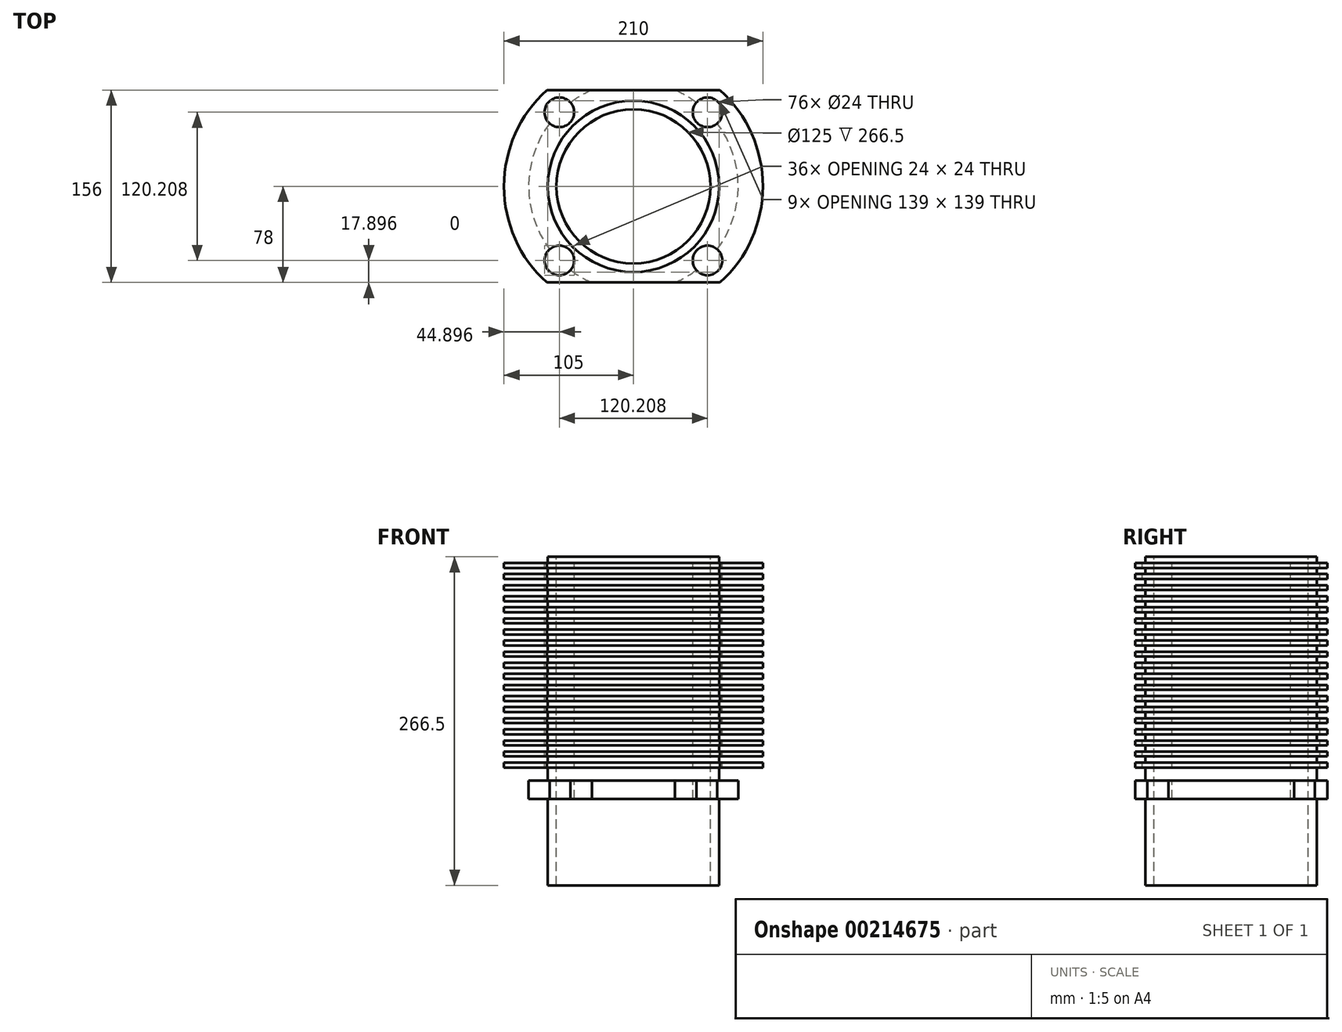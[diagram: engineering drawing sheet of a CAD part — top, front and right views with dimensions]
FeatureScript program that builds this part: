
annotation { "Feature Type Name" : "Feature", "Feature Type Description" : "" }
export const myFeature = defineFeature(function(context is Context, id is Id, definition is map)
    precondition{}
    {
        {
            var Q0;
            Q0=qCreatedBy(makeId("Top.planeOp"),FACE);
            var sketch = newSketch(context, id + "F0", { "sketchPlane" : qUnion([Q0])});
            skCircle(sketch, "E0", {"center": v(0, 0) * mm, "radius": 69.5 * mm});
            skCircle(sketch, "E1", {"center": v(0, 0) * mm, "radius": 62.5 * mm});
            skSolve(sketch);
        }
        {
            var Q0;
            Q0=makeQuery(id+"F0.imprint","IMPRINT",FACE,{"disambiguationData":[TD([[makeQuery(id+"F0.imprint","IMPRINT",EDGE,{"derivedFrom":sQuery(id+"F0.wireOp",EDGE,"E0")}),1.0]])]});
            extrude(context, id + "F1", {"entities" : qUnion([Q0]), "oppositeDirection" : true, "depth" : 266.5 * mm});
        }
        {
            var Q0;
            Q0=qCreatedBy(makeId("Front.planeOp"),FACE);
            var sketch = newSketch(context, id + "F2", { "sketchPlane" : qUnion([Q0])});
            skLineSegment(sketch, "E2", {"start": v(0, 0) * mm, "end": v(0, -266.5) * mm});
            skLineSegment(sketch, "E3", {"start": v(0, -196.5) * mm, "end": v(85, -196.5) * mm});
            skLineSegment(sketch, "E4", {"start": v(85, -196.5) * mm, "end": v(85, -181.5) * mm});
            skLineSegment(sketch, "E5", {"start": v(85, -181.5) * mm, "end": v(0, -181.5) * mm});
            skLineSegment(sketch, "E6", {"start": v(0, -5) * mm, "end": v(105, -5) * mm});
            skLineSegment(sketch, "E7", {"start": v(105, -5) * mm, "end": v(105, -9) * mm});
            skLineSegment(sketch, "E8", {"start": v(105, -9) * mm, "end": v(0, -9) * mm});
            skLineSegment(sketch, "E9.0.1.0", {"start": v(0, -14) * mm, "end": v(105, -14) * mm});
            skLineSegment(sketch, "E9.0.1.1", {"start": v(105, -18) * mm, "end": v(0, -18) * mm});
            skLineSegment(sketch, "E9.0.1.2", {"start": v(105, -14) * mm, "end": v(105, -18) * mm});
            skLineSegment(sketch, "E9.0.2.0", {"start": v(0, -23) * mm, "end": v(105, -23) * mm});
            skLineSegment(sketch, "E9.0.2.1", {"start": v(105, -27) * mm, "end": v(0, -27) * mm});
            skLineSegment(sketch, "E9.0.2.2", {"start": v(105, -23) * mm, "end": v(105, -27) * mm});
            skLineSegment(sketch, "E9.0.3.0", {"start": v(0, -32) * mm, "end": v(105, -32) * mm});
            skLineSegment(sketch, "E9.0.3.1", {"start": v(105, -36) * mm, "end": v(0, -36) * mm});
            skLineSegment(sketch, "E9.0.3.2", {"start": v(105, -32) * mm, "end": v(105, -36) * mm});
            skLineSegment(sketch, "E9.0.4.0", {"start": v(0, -41) * mm, "end": v(105, -41) * mm});
            skLineSegment(sketch, "E9.0.4.1", {"start": v(105, -45) * mm, "end": v(0, -45) * mm});
            skLineSegment(sketch, "E9.0.4.2", {"start": v(105, -41) * mm, "end": v(105, -45) * mm});
            skLineSegment(sketch, "E9.0.5.0", {"start": v(0, -50) * mm, "end": v(105, -50) * mm});
            skLineSegment(sketch, "E9.0.5.1", {"start": v(105, -54) * mm, "end": v(0, -54) * mm});
            skLineSegment(sketch, "E9.0.5.2", {"start": v(105, -50) * mm, "end": v(105, -54) * mm});
            skLineSegment(sketch, "E9.0.6.0", {"start": v(0, -59) * mm, "end": v(105, -59) * mm});
            skLineSegment(sketch, "E9.0.6.1", {"start": v(105, -63) * mm, "end": v(0, -63) * mm});
            skLineSegment(sketch, "E9.0.6.2", {"start": v(105, -59) * mm, "end": v(105, -63) * mm});
            skLineSegment(sketch, "E9.0.7.0", {"start": v(0, -68) * mm, "end": v(105, -68) * mm});
            skLineSegment(sketch, "E9.0.7.1", {"start": v(105, -72) * mm, "end": v(0, -72) * mm});
            skLineSegment(sketch, "E9.0.7.2", {"start": v(105, -68) * mm, "end": v(105, -72) * mm});
            skLineSegment(sketch, "E9.0.8.0", {"start": v(0, -77) * mm, "end": v(105, -77) * mm});
            skLineSegment(sketch, "E9.0.8.1", {"start": v(105, -81) * mm, "end": v(0, -81) * mm});
            skLineSegment(sketch, "E9.0.8.2", {"start": v(105, -77) * mm, "end": v(105, -81) * mm});
            skLineSegment(sketch, "E9.0.9.0", {"start": v(0, -86) * mm, "end": v(105, -86) * mm});
            skLineSegment(sketch, "E9.0.9.1", {"start": v(105, -90) * mm, "end": v(0, -90) * mm});
            skLineSegment(sketch, "E9.0.9.2", {"start": v(105, -86) * mm, "end": v(105, -90) * mm});
            skLineSegment(sketch, "E9.0.10.0", {"start": v(0, -95) * mm, "end": v(105, -95) * mm});
            skLineSegment(sketch, "E9.0.10.1", {"start": v(105, -99) * mm, "end": v(0, -99) * mm});
            skLineSegment(sketch, "E9.0.10.2", {"start": v(105, -95) * mm, "end": v(105, -99) * mm});
            skLineSegment(sketch, "E9.0.11.0", {"start": v(0, -104) * mm, "end": v(105, -104) * mm});
            skLineSegment(sketch, "E9.0.11.1", {"start": v(105, -108) * mm, "end": v(0, -108) * mm});
            skLineSegment(sketch, "E9.0.11.2", {"start": v(105, -104) * mm, "end": v(105, -108) * mm});
            skLineSegment(sketch, "E9.0.12.0", {"start": v(0, -113) * mm, "end": v(105, -113) * mm});
            skLineSegment(sketch, "E9.0.12.1", {"start": v(105, -117) * mm, "end": v(0, -117) * mm});
            skLineSegment(sketch, "E9.0.12.2", {"start": v(105, -113) * mm, "end": v(105, -117) * mm});
            skLineSegment(sketch, "E9.0.13.0", {"start": v(0, -122) * mm, "end": v(105, -122) * mm});
            skLineSegment(sketch, "E9.0.13.1", {"start": v(105, -126) * mm, "end": v(0, -126) * mm});
            skLineSegment(sketch, "E9.0.13.2", {"start": v(105, -122) * mm, "end": v(105, -126) * mm});
            skLineSegment(sketch, "E9.0.14.0", {"start": v(0, -131) * mm, "end": v(105, -131) * mm});
            skLineSegment(sketch, "E9.0.14.1", {"start": v(105, -135) * mm, "end": v(0, -135) * mm});
            skLineSegment(sketch, "E9.0.14.2", {"start": v(105, -131) * mm, "end": v(105, -135) * mm});
            skLineSegment(sketch, "E9.direction1", {"start": v(0, -5) * mm, "end": v(31, -5) * mm, "construction": true});
            skLineSegment(sketch, "E9.direction2", {"start": v(0, -5) * mm, "end": v(0, -14) * mm, "construction": true});
            skLineSegment(sketch, "E10.0.0.15", {"start": v(0, -140) * mm, "end": v(105, -140) * mm});
            skLineSegment(sketch, "E10.3.0.15", {"start": v(105, -144) * mm, "end": v(0, -144) * mm});
            skLineSegment(sketch, "E10.6.0.15", {"start": v(105, -140) * mm, "end": v(105, -144) * mm});
            skLineSegment(sketch, "E10.0.0.16", {"start": v(0, -149) * mm, "end": v(105, -149) * mm});
            skLineSegment(sketch, "E10.3.0.16", {"start": v(105, -153) * mm, "end": v(0, -153) * mm});
            skLineSegment(sketch, "E10.6.0.16", {"start": v(105, -149) * mm, "end": v(105, -153) * mm});
            skLineSegment(sketch, "E10.0.0.17", {"start": v(0, -158) * mm, "end": v(105, -158) * mm});
            skLineSegment(sketch, "E10.3.0.17", {"start": v(105, -162) * mm, "end": v(0, -162) * mm});
            skLineSegment(sketch, "E10.6.0.17", {"start": v(105, -158) * mm, "end": v(105, -162) * mm});
            skLineSegment(sketch, "E10.0.0.18", {"start": v(0, -167) * mm, "end": v(105, -167) * mm});
            skLineSegment(sketch, "E10.3.0.18", {"start": v(105, -171) * mm, "end": v(0, -171) * mm});
            skLineSegment(sketch, "E10.6.0.18", {"start": v(105, -167) * mm, "end": v(105, -171) * mm});
            skSolve(sketch);
        }
        {
            var Q0;
            {var subQ0=sQuery(id+"F2.wireOp",EDGE,"E3");Q0=makeQuery(id+"F2.imprint","IMPRINT",FACE,{"disambiguationData":[TD([[makeQuery(id+"F2.imprint","IMPRINT",EDGE,{"derivedFrom":subQ0}),1.0]])]});}
            var Q1;
            {var subQ0=sQuery(id+"F2.wireOp",EDGE,"E10.0.0.18");Q1=makeQuery(id+"F2.imprint","IMPRINT",FACE,{"disambiguationData":[TD([[makeQuery(id+"F2.imprint","IMPRINT",EDGE,{"derivedFrom":subQ0}),-1.0]])]});}
            var Q2;
            {var subQ0=sQuery(id+"F2.wireOp",EDGE,"E10.0.0.17");Q2=makeQuery(id+"F2.imprint","IMPRINT",FACE,{"disambiguationData":[TD([[makeQuery(id+"F2.imprint","IMPRINT",EDGE,{"derivedFrom":subQ0}),-1.0]])]});}
            var Q3;
            {var subQ0=sQuery(id+"F2.wireOp",EDGE,"E10.0.0.16");Q3=makeQuery(id+"F2.imprint","IMPRINT",FACE,{"disambiguationData":[TD([[makeQuery(id+"F2.imprint","IMPRINT",EDGE,{"derivedFrom":subQ0}),-1.0]])]});}
            var Q4;
            {var subQ0=sQuery(id+"F2.wireOp",EDGE,"E10.0.0.15");Q4=makeQuery(id+"F2.imprint","IMPRINT",FACE,{"disambiguationData":[TD([[makeQuery(id+"F2.imprint","IMPRINT",EDGE,{"derivedFrom":subQ0}),-1.0]])]});}
            var Q5;
            {var subQ0=sQuery(id+"F2.wireOp",EDGE,"E9.0.14.0");Q5=makeQuery(id+"F2.imprint","IMPRINT",FACE,{"disambiguationData":[TD([[makeQuery(id+"F2.imprint","IMPRINT",EDGE,{"derivedFrom":subQ0}),-1.0]])]});}
            var Q6;
            {var subQ0=sQuery(id+"F2.wireOp",EDGE,"E9.0.13.0");Q6=makeQuery(id+"F2.imprint","IMPRINT",FACE,{"disambiguationData":[TD([[makeQuery(id+"F2.imprint","IMPRINT",EDGE,{"derivedFrom":subQ0}),-1.0]])]});}
            var Q7;
            {var subQ0=sQuery(id+"F2.wireOp",EDGE,"E9.0.12.0");Q7=makeQuery(id+"F2.imprint","IMPRINT",FACE,{"disambiguationData":[TD([[makeQuery(id+"F2.imprint","IMPRINT",EDGE,{"derivedFrom":subQ0}),-1.0]])]});}
            var Q8;
            {var subQ0=sQuery(id+"F2.wireOp",EDGE,"E9.0.11.0");Q8=makeQuery(id+"F2.imprint","IMPRINT",FACE,{"disambiguationData":[TD([[makeQuery(id+"F2.imprint","IMPRINT",EDGE,{"derivedFrom":subQ0}),-1.0]])]});}
            var Q9;
            {var subQ0=sQuery(id+"F2.wireOp",EDGE,"E9.0.10.0");Q9=makeQuery(id+"F2.imprint","IMPRINT",FACE,{"disambiguationData":[TD([[makeQuery(id+"F2.imprint","IMPRINT",EDGE,{"derivedFrom":subQ0}),-1.0]])]});}
            var Q10;
            {var subQ0=sQuery(id+"F2.wireOp",EDGE,"E9.0.9.0");Q10=makeQuery(id+"F2.imprint","IMPRINT",FACE,{"disambiguationData":[TD([[makeQuery(id+"F2.imprint","IMPRINT",EDGE,{"derivedFrom":subQ0}),-1.0]])]});}
            var Q11;
            {var subQ0=sQuery(id+"F2.wireOp",EDGE,"E9.0.8.0");Q11=makeQuery(id+"F2.imprint","IMPRINT",FACE,{"disambiguationData":[TD([[makeQuery(id+"F2.imprint","IMPRINT",EDGE,{"derivedFrom":subQ0}),-1.0]])]});}
            var Q12;
            {var subQ0=sQuery(id+"F2.wireOp",EDGE,"E9.0.7.0");Q12=makeQuery(id+"F2.imprint","IMPRINT",FACE,{"disambiguationData":[TD([[makeQuery(id+"F2.imprint","IMPRINT",EDGE,{"derivedFrom":subQ0}),-1.0]])]});}
            var Q13;
            {var subQ0=sQuery(id+"F2.wireOp",EDGE,"E9.0.6.0");Q13=makeQuery(id+"F2.imprint","IMPRINT",FACE,{"disambiguationData":[TD([[makeQuery(id+"F2.imprint","IMPRINT",EDGE,{"derivedFrom":subQ0}),-1.0]])]});}
            var Q14;
            {var subQ0=sQuery(id+"F2.wireOp",EDGE,"E9.0.5.0");Q14=makeQuery(id+"F2.imprint","IMPRINT",FACE,{"disambiguationData":[TD([[makeQuery(id+"F2.imprint","IMPRINT",EDGE,{"derivedFrom":subQ0}),-1.0]])]});}
            var Q15;
            {var subQ0=sQuery(id+"F2.wireOp",EDGE,"E9.0.4.0");Q15=makeQuery(id+"F2.imprint","IMPRINT",FACE,{"disambiguationData":[TD([[makeQuery(id+"F2.imprint","IMPRINT",EDGE,{"derivedFrom":subQ0}),-1.0]])]});}
            var Q16;
            {var subQ0=sQuery(id+"F2.wireOp",EDGE,"E9.0.3.0");Q16=makeQuery(id+"F2.imprint","IMPRINT",FACE,{"disambiguationData":[TD([[makeQuery(id+"F2.imprint","IMPRINT",EDGE,{"derivedFrom":subQ0}),-1.0]])]});}
            var Q17;
            {var subQ0=sQuery(id+"F2.wireOp",EDGE,"E9.0.2.0");Q17=makeQuery(id+"F2.imprint","IMPRINT",FACE,{"disambiguationData":[TD([[makeQuery(id+"F2.imprint","IMPRINT",EDGE,{"derivedFrom":subQ0}),-1.0]])]});}
            var Q18;
            {var subQ0=sQuery(id+"F2.wireOp",EDGE,"E9.0.1.0");Q18=makeQuery(id+"F2.imprint","IMPRINT",FACE,{"disambiguationData":[TD([[makeQuery(id+"F2.imprint","IMPRINT",EDGE,{"derivedFrom":subQ0}),-1.0]])]});}
            var Q19;
            {var subQ0=sQuery(id+"F2.wireOp",EDGE,"E6");Q19=makeQuery(id+"F2.imprint","IMPRINT",FACE,{"disambiguationData":[TD([[makeQuery(id+"F2.imprint","IMPRINT",EDGE,{"derivedFrom":subQ0}),-1.0]])]});}
            var Q20;
            Q20=sQuery(id+"F2.wireOp",EDGE,"E2");
            revolve(context, id + "F3", {"operationType" : NewBodyOperationType.ADD, "entities" : qUnion([Q0, Q1, Q2, Q3, Q4, Q5, Q6, Q7, Q8, Q9, Q10, Q11, Q12, Q13, Q14, Q15, Q16, Q17, Q18, Q19]), "axis" : qUnion([Q20]), "revolveType" : RevolveType.FULL});
        }
        {
            var Q0;
            Q0=makeQuery(id+"F0.imprint","IMPRINT",FACE,{"disambiguationData":[TD([[makeQuery(id+"F0.imprint","IMPRINT",EDGE,{"derivedFrom":sQuery(id+"F0.wireOp",EDGE,"E1")}),1.0]])]});
            var Q1;
            Q1=sQuery(id+"F0.wireOp",EDGE,"E1");
            extrude(context, id + "F4", {"entities" : qUnion([Q0]), "operationType" : NewBodyOperationType.REMOVE, "surfaceEntities" : qUnion([Q1]), "oppositeDirection" : true, "depth" : 300 * mm});
        }
        {
            var Q0;
            Q0=qCreatedBy(makeId("Top.planeOp"),FACE);
            cPlane(context, id + "F5", {"entities" : qUnion([Q0]), "cplaneType" : CPlaneType.OFFSET, "offset" : 25 * mm, "width" : 150 * mm, "height" : 150 * mm});
        }
        {
            var Q0;
            Q0=qCreatedBy(id+"F5.planeOp",FACE);
            var sketch = newSketch(context, id + "F6", { "sketchPlane" : qUnion([Q0])});
            skLineSegment(sketch, "E11.bottom", {"start": v(125, 78) * mm, "end": v(-125, 78) * mm});
            skLineSegment(sketch, "E11.top", {"start": v(125, -78) * mm, "end": v(-125, -78) * mm});
            skLineSegment(sketch, "E11.left", {"start": v(125, 78) * mm, "end": v(125, -78) * mm});
            skLineSegment(sketch, "E11.right", {"start": v(-125, 78) * mm, "end": v(-125, -78) * mm});
            skLineSegment(sketch, "E12", {"start": v(0, 0) * mm, "end": v(-30.4, 0) * mm});
            skLineSegment(sketch, "E13.bottom", {"start": v(169.14, 132.13) * mm, "end": v(-146.14, 132.13) * mm});
            skLineSegment(sketch, "E13.top", {"start": v(169.14, -135.37) * mm, "end": v(-146.14, -135.37) * mm});
            skLineSegment(sketch, "E13.left", {"start": v(169.14, 132.13) * mm, "end": v(169.14, -135.37) * mm});
            skLineSegment(sketch, "E13.right", {"start": v(-146.14, 132.13) * mm, "end": v(-146.14, -135.37) * mm});
            skSolve(sketch);
        }
        {
            var Q0;
            Q0=makeQuery(id+"F6.imprint","IMPRINT",FACE,{"disambiguationData":[TD([[makeQuery(id+"F6.imprint","IMPRINT",EDGE,{"derivedFrom":sQuery(id+"F6.wireOp",EDGE,"E11.bottom")}),-1.0]])]});
            extrude(context, id + "F7", {"entities" : qUnion([Q0]), "operationType" : NewBodyOperationType.REMOVE, "oppositeDirection" : true, "depth" : 250 * mm});
        }
        {
            var Q0;
            Q0=qCreatedBy(id+"F5.planeOp",FACE);
            var sketch = newSketch(context, id + "F8", { "sketchPlane" : qUnion([Q0])});
            skCircle(sketch, "E14", {"center": v(0, 0) * mm, "radius": 85 * mm});
            skCircle(sketch, "E15", {"center": v(-85, 0) * mm, "radius": 12 * mm});
            skCircle(sketch, "E16.1.0", {"center": v(-60.1, -60.1) * mm, "radius": 12 * mm});
            skCircle(sketch, "E16.2.0", {"center": v(0, -85) * mm, "radius": 12 * mm});
            skCircle(sketch, "E16.3.0", {"center": v(60.1, -60.1) * mm, "radius": 12 * mm});
            skCircle(sketch, "E16.4.0", {"center": v(85, 0) * mm, "radius": 12 * mm});
            skCircle(sketch, "E16.5.0", {"center": v(60.1, 60.1) * mm, "radius": 12 * mm});
            skCircle(sketch, "E16.6.0", {"center": v(0, 85) * mm, "radius": 12 * mm});
            skCircle(sketch, "E16.7.0", {"center": v(-60.1, 60.1) * mm, "radius": 12 * mm});
            skSolve(sketch);
        }
        {
            var Q0;
            {var subQ0=sQuery(id+"F8.wireOp",EDGE,"E16.3.0");var subQ1=sQuery(id+"F8.wireOp",EDGE,"E14");var subQ2=makeQuery(id+"F8.imprint","INTERSECT",VERTEX,{"disambiguationData":[OD(0.0)],"derivedFrom":[subQ1,subQ0]});Q0=makeQuery(id+"F8.imprint","IMPRINT",FACE,{"disambiguationData":[TD([[makeQuery(id+"F8.imprint","IMPRINT",EDGE,{"disambiguationData":[TD([[subQ2,-1.0]])],"derivedFrom":subQ1}),-1.0]])]});}
            var Q1;
            {var subQ0=sQuery(id+"F8.wireOp",EDGE,"E16.3.0");var subQ1=sQuery(id+"F8.wireOp",EDGE,"E14");var subQ2=makeQuery(id+"F8.imprint","INTERSECT",VERTEX,{"disambiguationData":[OD(0.0)],"derivedFrom":[subQ1,subQ0]});Q1=makeQuery(id+"F8.imprint","IMPRINT",FACE,{"disambiguationData":[TD([[makeQuery(id+"F8.imprint","IMPRINT",EDGE,{"disambiguationData":[TD([[subQ2,-1.0]])],"derivedFrom":subQ1}),1.0]])]});}
            var Q2;
            {var subQ0=sQuery(id+"F8.wireOp",EDGE,"E16.1.0");var subQ1=sQuery(id+"F8.wireOp",EDGE,"E14");var subQ2=makeQuery(id+"F8.imprint","INTERSECT",VERTEX,{"disambiguationData":[OD(0.0)],"derivedFrom":[subQ1,subQ0]});Q2=makeQuery(id+"F8.imprint","IMPRINT",FACE,{"disambiguationData":[TD([[makeQuery(id+"F8.imprint","IMPRINT",EDGE,{"disambiguationData":[TD([[subQ2,-1.0]])],"derivedFrom":subQ1}),-1.0]])]});}
            var Q3;
            {var subQ0=sQuery(id+"F8.wireOp",EDGE,"E16.1.0");var subQ1=sQuery(id+"F8.wireOp",EDGE,"E14");var subQ2=makeQuery(id+"F8.imprint","INTERSECT",VERTEX,{"disambiguationData":[OD(0.0)],"derivedFrom":[subQ1,subQ0]});Q3=makeQuery(id+"F8.imprint","IMPRINT",FACE,{"disambiguationData":[TD([[makeQuery(id+"F8.imprint","IMPRINT",EDGE,{"disambiguationData":[TD([[subQ2,-1.0]])],"derivedFrom":subQ1}),1.0]])]});}
            var Q4;
            {var subQ0=sQuery(id+"F8.wireOp",EDGE,"E16.7.0");var subQ1=sQuery(id+"F8.wireOp",EDGE,"E14");var subQ2=makeQuery(id+"F8.imprint","INTERSECT",VERTEX,{"disambiguationData":[OD(0.0)],"derivedFrom":[subQ1,subQ0]});Q4=makeQuery(id+"F8.imprint","IMPRINT",FACE,{"disambiguationData":[TD([[makeQuery(id+"F8.imprint","IMPRINT",EDGE,{"disambiguationData":[TD([[subQ2,-1.0]])],"derivedFrom":subQ1}),-1.0]])]});}
            var Q5;
            {var subQ0=sQuery(id+"F8.wireOp",EDGE,"E16.7.0");var subQ1=sQuery(id+"F8.wireOp",EDGE,"E14");var subQ2=makeQuery(id+"F8.imprint","INTERSECT",VERTEX,{"disambiguationData":[OD(0.0)],"derivedFrom":[subQ1,subQ0]});Q5=makeQuery(id+"F8.imprint","IMPRINT",FACE,{"disambiguationData":[TD([[makeQuery(id+"F8.imprint","IMPRINT",EDGE,{"disambiguationData":[TD([[subQ2,-1.0]])],"derivedFrom":subQ1}),1.0]])]});}
            var Q6;
            {var subQ0=sQuery(id+"F8.wireOp",EDGE,"E16.5.0");var subQ1=sQuery(id+"F8.wireOp",EDGE,"E14");var subQ2=makeQuery(id+"F8.imprint","INTERSECT",VERTEX,{"disambiguationData":[OD(0.0)],"derivedFrom":[subQ1,subQ0]});Q6=makeQuery(id+"F8.imprint","IMPRINT",FACE,{"disambiguationData":[TD([[makeQuery(id+"F8.imprint","IMPRINT",EDGE,{"disambiguationData":[TD([[subQ2,-1.0]])],"derivedFrom":subQ1}),-1.0]])]});}
            var Q7;
            {var subQ0=sQuery(id+"F8.wireOp",EDGE,"E16.5.0");var subQ1=sQuery(id+"F8.wireOp",EDGE,"E14");var subQ2=makeQuery(id+"F8.imprint","INTERSECT",VERTEX,{"disambiguationData":[OD(0.0)],"derivedFrom":[subQ1,subQ0]});Q7=makeQuery(id+"F8.imprint","IMPRINT",FACE,{"disambiguationData":[TD([[makeQuery(id+"F8.imprint","IMPRINT",EDGE,{"disambiguationData":[TD([[subQ2,-1.0]])],"derivedFrom":subQ1}),1.0]])]});}
            extrude(context, id + "F9", {"entities" : qUnion([Q0, Q1, Q2, Q3, Q4, Q5, Q6, Q7]), "operationType" : NewBodyOperationType.REMOVE, "oppositeDirection" : true, "depth" : 250 * mm});
        }
    });
